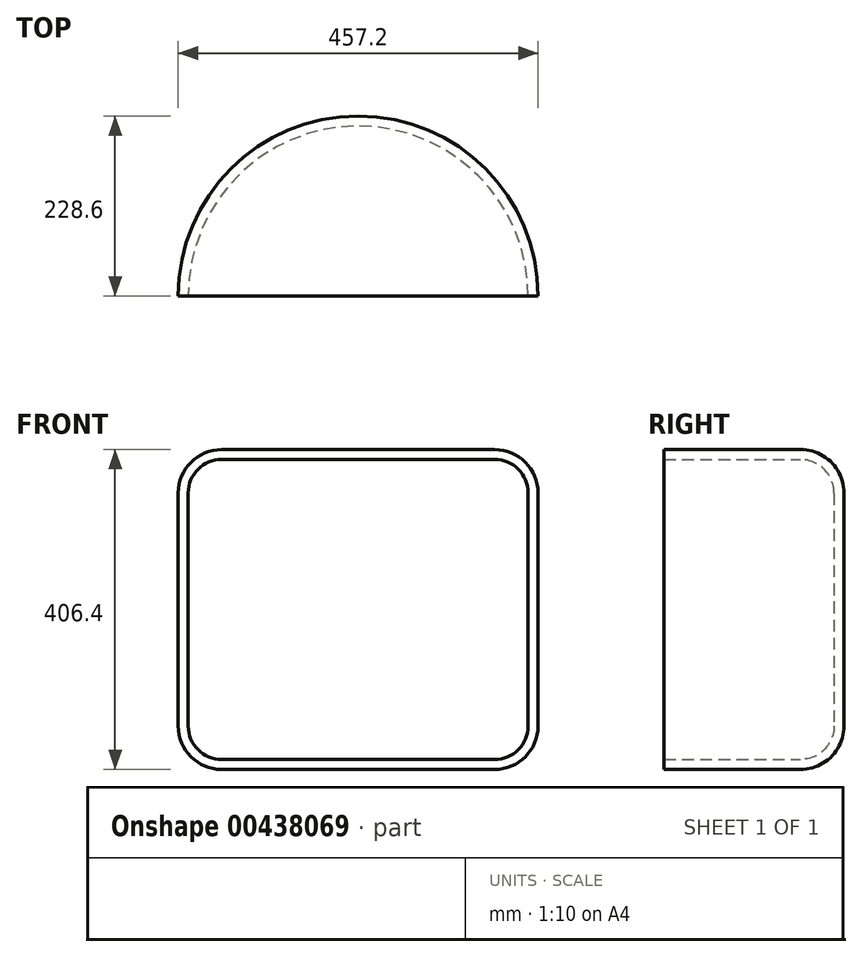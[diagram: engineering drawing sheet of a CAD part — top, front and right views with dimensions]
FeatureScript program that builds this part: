
annotation { "Feature Type Name" : "Feature", "Feature Type Description" : "" }
export const myFeature = defineFeature(function(context is Context, id is Id, definition is map)
    precondition{}
    {
        {
            var Q0;
            Q0=qCreatedBy(makeId("Top.planeOp"),FACE);
            var sketch = newSketch(context, id + "F0", { "sketchPlane" : qUnion([Q0])});
            skArc(sketch, "E0", {"start": v(-228.6, 0) * mm, "mid": v(0, 228.6) * mm, "end": v(228.6, 0) * mm});
            skLineSegment(sketch, "E1", {"start": v(-228.6, 0) * mm, "end": v(228.6, 0) * mm});
            skSolve(sketch);
        }
        {
            var Q0;
            Q0 = qSketchRegion(id + "F0", true);
            var Q1;
            Q1=makeQuery(id+"F0.imprint","IMPRINT",FACE,{"disambiguationData":[TD([[makeQuery(id+"F0.imprint","IMPRINT",EDGE,{"derivedFrom":sQuery(id+"F0.wireOp",EDGE,"E0")}),-1.0]])]});
            extrude(context, id + "F1", {"entities" : qUnion([Q0, Q1]), "depth" : 406.4 * mm});
        }
        {
            var Q0;
            Q0=makeQuery(id+"F1.opExtrude","CAP_EDGE",EDGE,{"disambiguationData":[OSD([sQuery(id+"F0.wireOp",EDGE,"E0")])],"isStart":false});
            var Q1;
            {var subQ0=sQuery(id+"F0.wireOp",EDGE,"E0");Q1=makeQuery(id+"FoSRKTeVG2OO3q8_1.opShell","OFFSET_EDGE",EDGE,{"disambiguationData":[OSD([subQ0]),TDD([makeQuery(id+"F1.opExtrude","CAP_EDGE",EDGE,{"disambiguationData":[OSD([subQ0])],"isStart":false})])]});}
            fillet(context, id + "F2", {"entities" : qUnion([Q0, Q1]), "radius" : 55.2 * mm, "tangentPropagation" : true, "allowEdgeOverflow" : false});
        }
        {
            var Q0;
            Q0=makeQuery(id+"F1.opExtrude","CAP_EDGE",EDGE,{"disambiguationData":[OSD([sQuery(id+"F0.wireOp",EDGE,"E0")])],"isStart":true});
            fillet(context, id + "F3", {"entities" : qUnion([Q0]), "radius" : 55.2 * mm, "tangentPropagation" : true, "allowEdgeOverflow" : false});
        }
        {
            var Q0;
            Q0=makeQuery(id+"F1.opExtrude","SWEPT_FACE",FACE,{"disambiguationData":[OSD([sQuery(id+"F0.wireOp",EDGE,"E1")])]});
            shell(context, id + "F4", {"entities" : qUnion([Q0]), "thickness" : 12.7 * mm});
        }
    });
